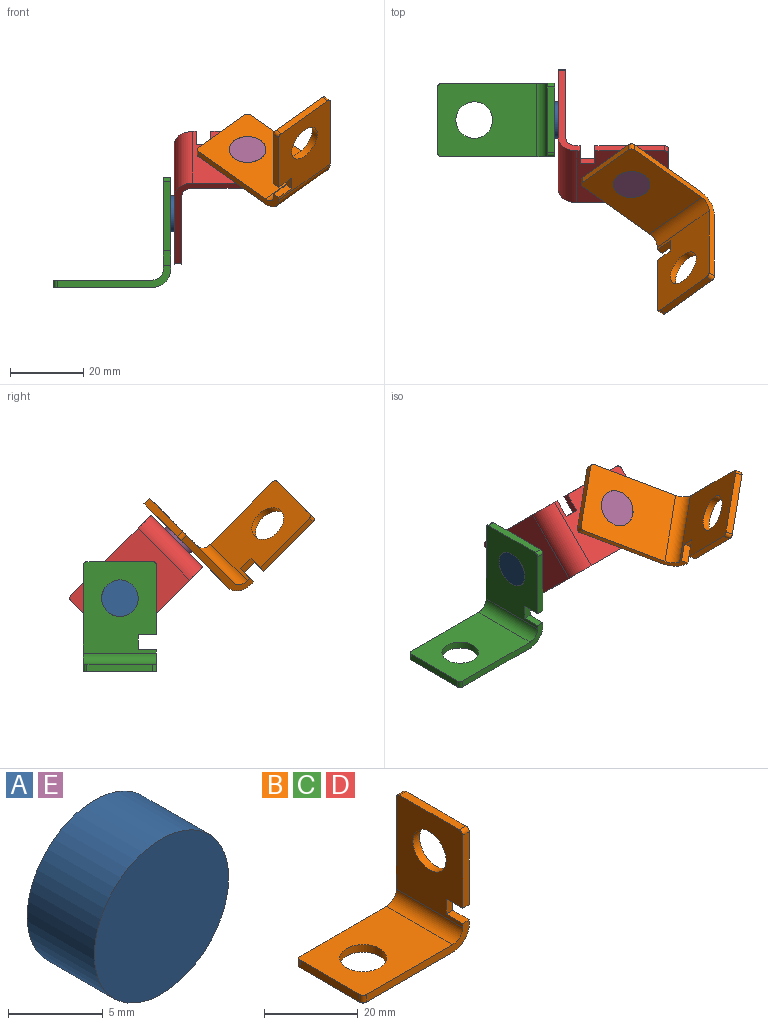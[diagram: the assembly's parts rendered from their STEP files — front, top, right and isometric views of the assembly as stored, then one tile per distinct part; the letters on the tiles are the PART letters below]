
ASSEMBLY  parts=5 mates=4
PART A: 3 faces, bbox 10x5x10 mm
  f0: cylinder r=5mm len=10mm, axis (0,1,0), area 157.1mm2, adj f1,f2
  f1: plane 10x10mm, normal (0,-1,0), area 78.5mm2, adj f0
  f2: plane 10x10mm, normal (0,1,0), area 78.5mm2, adj f0
PART B: 20 faces, bbox 32x20x30 mm
  f0: plane 25x20mm, normal (-1,0,0), area 401mm2, adj f1,f5,f6,f9,f10,f11,f12,f13
  f1: plane 19x2mm, normal (0,-1,0), area 38mm2, adj f0,f4,f11,f18
  f2: plane 27x20mm, normal (0,0,-1), area 461mm2, adj f3,f8,f9,f10,f15,f17,f19
  f3: cylinder r=5mm len=20mm, axis (0,1,0), area 157.1mm2, adj f2,f4,f9,f10
  f4: plane 25x20mm, normal (1,0,0), area 401mm2, adj f1,f3,f5,f9,f10,f11,f12,f13
  f5: plane 18x2mm, normal (0,0,1), area 36mm2, adj f0,f4,f16,f18
  f6: cylinder r=3mm len=20mm, axis (0,1,0), area 94.2mm2, adj f0,f7,f9,f10
  f7: plane 27x20mm, normal (0,0,1), area 461mm2, adj f6,f8,f9,f10,f15,f17,f19
  f8: plane 18x2mm, normal (-1,0,0), area 36mm2, adj f2,f7,f17,f19
  f9: plane 31x6mm, normal (0,-1,0), area 66.6mm2, adj f0,f2,f3,f4,f6,f7,f12,f19
  f10: plane 31x29mm, normal (0,1,0), area 112.6mm2, adj f0,f2,f3,f4,f6,f7,f16,f17
  f11: plane 5x2mm, normal (0,0,-1), area 10mm2, adj f0,f1,f4,f13
  f12: plane 5x2mm, normal (0,0,1), area 10mm2, adj f0,f4,f9,f13
  f13: plane 4x2mm, normal (0,-1,0), area 8mm2, adj f0,f4,f11,f12
  f14: cylinder r=5mm len=10mm, axis (1,0,0), area 62.8mm2, adj f0,f4
  f15: cylinder r=5mm len=10mm, axis (0,0,-1), area 62.8mm2, adj f2,f7
  f16: cylinder r=1mm len=2mm, axis (-1,0,0), area 3.1mm2, adj f0,f4,f5,f10
  f17: cylinder r=1mm len=2mm, axis (0,0,-1), area 3.1mm2, adj f2,f7,f8,f10
  f18: cylinder r=1mm len=2mm, axis (1,0,0), area 3.1mm2, adj f0,f1,f4,f5
  f19: cylinder r=1mm len=2mm, axis (0,0,1), area 3.1mm2, adj f2,f7,f8,f9
PART C: same geometry as B
PART D: same geometry as B
PART E: same geometry as A
PLACE A rot(axis=(-0.58,-0.58,-0.58),120deg) t=(-38.72,-87.21,75.36)mm
PLACE B rot(axis=(0.68,0.28,-0.68),62.8deg) t=(19.13,-86.35,35.55)mm
PLACE C t=(-17.36,-17.77,27.47)mm fixed
PLACE D rot(axis=(-0.68,0.28,-0.68),148.6deg) t=(-6.58,-67.62,39.03)mm
PLACE E rot(axis=(1,0,0),135deg) t=(41.31,-3.42,73.04)mm
MATE fastened E.f0 <-> B.f15  axis (0,-0.71,0.71) through (-20.72,-45.45,31)mm
MATE fastened E.f0 <-> D.f14  axis (0,0.71,-0.71) through (-20.72,-41.92,27.47)mm
MATE fastened A.f0 <-> D.f15  axis (1,0,0) through (-38.72,-27.77,13.33)mm
MATE fastened A.f0 <-> C.f14  axis (-1,0,0) through (-43.72,-27.77,13.33)mm
